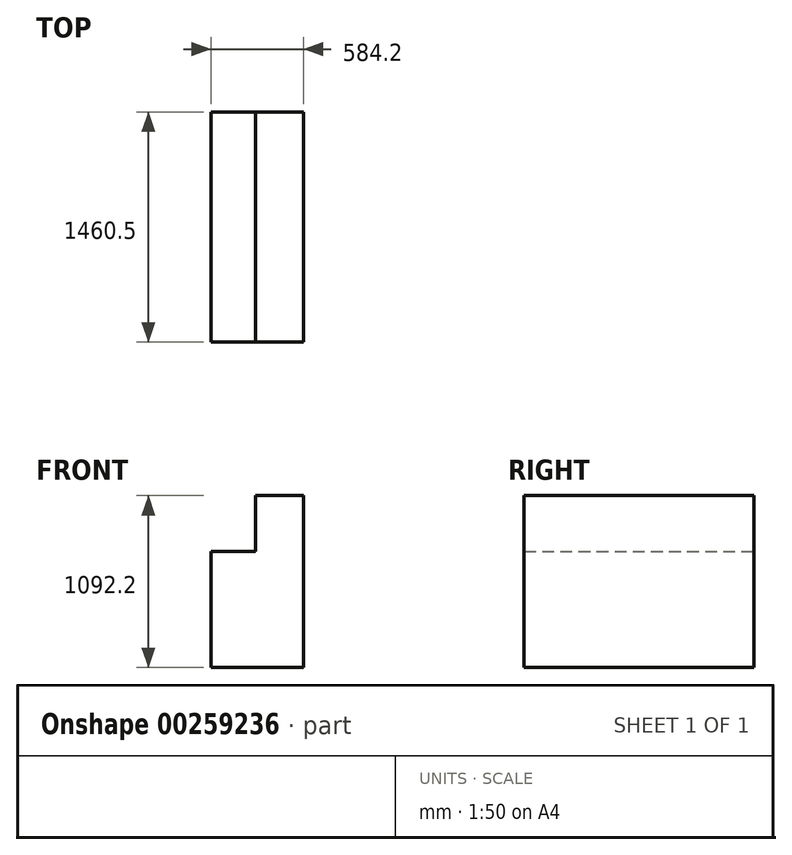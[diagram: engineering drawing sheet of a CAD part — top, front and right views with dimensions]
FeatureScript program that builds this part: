
annotation { "Feature Type Name" : "Feature", "Feature Type Description" : "" }
export const myFeature = defineFeature(function(context is Context, id is Id, definition is map)
    precondition{}
    {
        {
            var Q0;
            Q0=qCreatedBy(makeId("Front.planeOp"),FACE);
            var sketch = newSketch(context, id + "F0", { "sketchPlane" : qUnion([Q0])});
            skLineSegment(sketch, "E0", {"start": v(-56.34, 49.98) * mm, "end": v(248.46, 49.98) * mm});
            skLineSegment(sketch, "E1", {"start": v(248.46, 49.98) * mm, "end": v(248.46, -1042.22) * mm});
            skLineSegment(sketch, "E2", {"start": v(248.46, -1042.22) * mm, "end": v(-335.74, -1042.22) * mm});
            skLineSegment(sketch, "E3", {"start": v(-335.74, -1042.22) * mm, "end": v(-335.74, -305.62) * mm});
            skLineSegment(sketch, "E4", {"start": v(-335.74, -305.62) * mm, "end": v(-56.34, -305.62) * mm});
            skLineSegment(sketch, "E5", {"start": v(-56.34, -305.62) * mm, "end": v(-56.34, 49.98) * mm});
            skSolve(sketch);
        }
        {
            var Q0;
            Q0=makeQuery(id+"F0.imprint","IMPRINT",FACE,{"disambiguationData":[TD([[makeQuery(id+"F0.imprint","IMPRINT",EDGE,{"derivedFrom":sQuery(id+"F0.wireOp",EDGE,"E0")}),-1.0]])]});
            extrude(context, id + "F1", {"entities" : qUnion([Q0]), "depth" : 1460.5 * mm});
        }
    });
